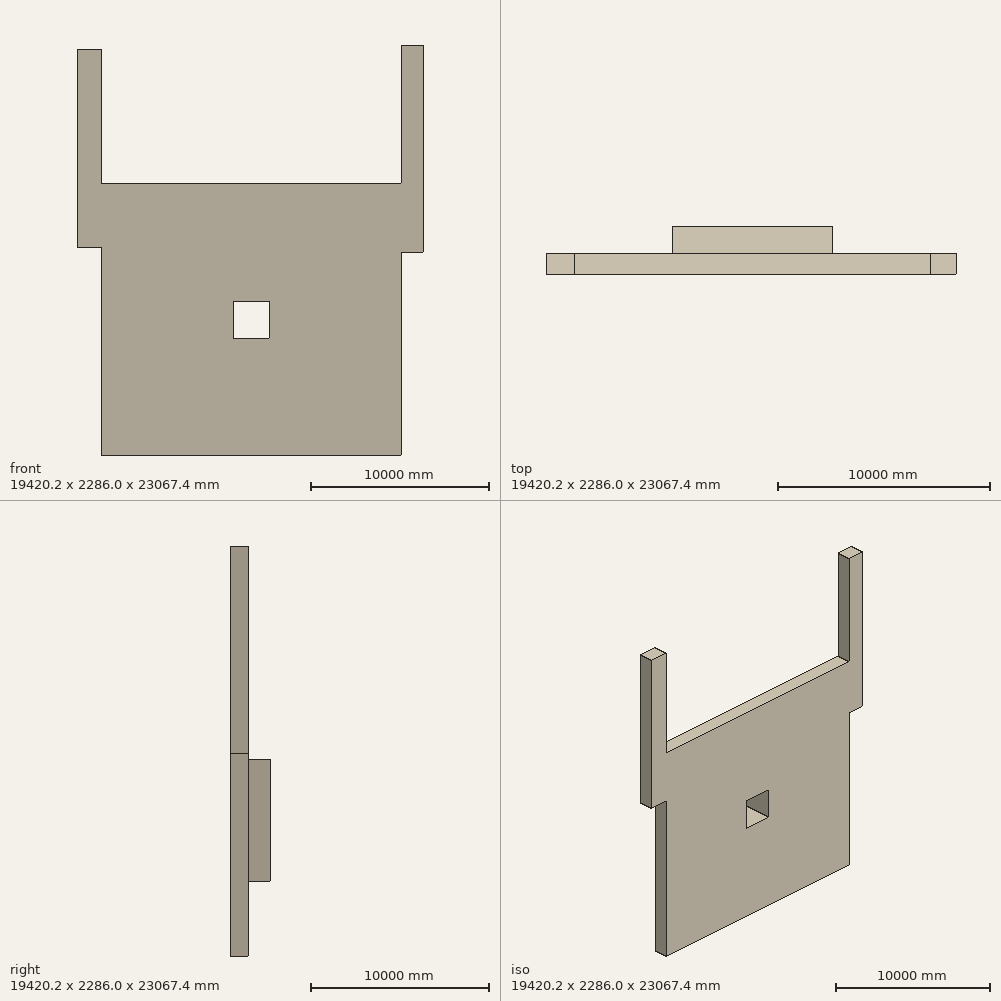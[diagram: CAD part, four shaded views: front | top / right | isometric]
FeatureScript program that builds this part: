
annotation { "Feature Type Name" : "Feature", "Feature Type Description" : "" }
export const myFeature = defineFeature(function(context is Context, id is Id, definition is map)
    precondition{}
    {
        {
            var Q0;
            Q0=qCreatedBy(makeId("Front.planeOp"),FACE);
            var sketch = newSketch(context, id + "F0", { "sketchPlane" : qUnion([Q0])});
            skLineSegment(sketch, "E0.bottom", {"start": v(1035, 1036.8) * mm, "end": v(-1035, 1036.8) * mm});
            skLineSegment(sketch, "E0.top", {"start": v(1035, -1036.8) * mm, "end": v(-1035, -1036.8) * mm});
            skLineSegment(sketch, "E0.left", {"start": v(1035, 1036.8) * mm, "end": v(1035, -1036.8) * mm});
            skLineSegment(sketch, "E0.right", {"start": v(-1035, 1036.8) * mm, "end": v(-1035, -1036.8) * mm});
            skPoint(sketch, "E0.middle", {"position": v(0, 0) * mm});
            skLineSegment(sketch, "E1.bottom", {"start": v(2390.28, 2208.64) * mm, "end": v(-2390.28, 2208.64) * mm});
            skLineSegment(sketch, "E1.top", {"start": v(2390.28, -2208.64) * mm, "end": v(-2390.28, -2208.64) * mm});
            skLineSegment(sketch, "E1.left", {"start": v(2390.28, 2208.64) * mm, "end": v(2390.28, -2208.64) * mm});
            skLineSegment(sketch, "E1.right", {"start": v(-2390.28, 2208.64) * mm, "end": v(-2390.28, -2208.64) * mm});
            skLineSegment(sketch, "E2.bottom", {"start": v(3793.65, 3412.2) * mm, "end": v(-3793.65, 3412.2) * mm});
            skLineSegment(sketch, "E2.top", {"start": v(3793.65, -3412.2) * mm, "end": v(-3793.65, -3412.2) * mm});
            skLineSegment(sketch, "E2.left", {"start": v(3793.65, 3412.2) * mm, "end": v(3793.65, -3412.2) * mm});
            skLineSegment(sketch, "E2.right", {"start": v(-3793.65, 3412.2) * mm, "end": v(-3793.65, -3412.2) * mm});
            skLineSegment(sketch, "E3.bottom", {"start": v(6075.26, 5902.37) * mm, "end": v(-6075.26, 5902.37) * mm});
            skLineSegment(sketch, "E3.top", {"start": v(6075.26, -5902.37) * mm, "end": v(-6075.26, -5902.37) * mm});
            skLineSegment(sketch, "E3.left", {"start": v(6075.26, 5902.37) * mm, "end": v(6075.26, -5902.37) * mm});
            skLineSegment(sketch, "E3.right", {"start": v(-6075.26, 5902.37) * mm, "end": v(-6075.26, -5902.37) * mm});
            skLineSegment(sketch, "E4.bottom", {"start": v(9651.79, 3795.28) * mm, "end": v(8437.94, 3795.28) * mm});
            skLineSegment(sketch, "E4.top", {"start": v(9651.79, 15422.85) * mm, "end": v(8437.94, 15422.85) * mm});
            skLineSegment(sketch, "E4.left", {"start": v(9651.79, 3795.28) * mm, "end": v(9651.79, 15422.85) * mm});
            skLineSegment(sketch, "E4.right", {"start": v(8437.94, 3795.28) * mm, "end": v(8437.94, 15422.85) * mm});
            skPoint(sketch, "E4.middle", {"position": v(9044.86, 9609.06) * mm});
            skLineSegment(sketch, "E5.bottom", {"start": v(8437.94, 7644.55) * mm, "end": v(-8437.94, 7644.55) * mm});
            skLineSegment(sketch, "E5.top", {"start": v(8437.94, -7644.55) * mm, "end": v(-8437.94, -7644.55) * mm});
            skLineSegment(sketch, "E5.left", {"start": v(8437.94, 7644.55) * mm, "end": v(8437.94, -7644.55) * mm});
            skLineSegment(sketch, "E5.right", {"start": v(-8437.94, 7644.55) * mm, "end": v(-8437.94, -7644.55) * mm});
            skLineSegment(sketch, "E6.bottom", {"start": v(-8437.94, 4040.6) * mm, "end": v(-9768.38, 4040.6) * mm});
            skLineSegment(sketch, "E6.top", {"start": v(-8437.94, 15177.53) * mm, "end": v(-9768.38, 15177.53) * mm});
            skLineSegment(sketch, "E6.left", {"start": v(-8437.94, 4040.6) * mm, "end": v(-8437.94, 15177.53) * mm});
            skLineSegment(sketch, "E6.right", {"start": v(-9768.38, 4040.6) * mm, "end": v(-9768.38, 15177.53) * mm});
            skPoint(sketch, "E6.middle", {"position": v(-9103.16, 9609.06) * mm});
            skPoint(sketch, "E6.middle.positionSnap0", {"position": v(8437.94, 9609.06) * mm});
            skPoint(sketch, "E6.centerSnap0", {"position": v(8437.94, 9609.06) * mm});
            skPoint(sketch, "E7.end.orphan", {"position": v(-8437.94, -12888.31) * mm});
            skPoint(sketch, "E8.end.orphan", {"position": v(-7547.34, -12888.31) * mm});
            skPoint(sketch, "E8.start.orphan", {"position": v(-7547.34, -7644.55) * mm});
            skSolve(sketch);
        }
        {
            var Q0;
            Q0 = qSketchRegion(id + "F0", true);
            var Q1;
            Q1=makeQuery(id+"F0.imprint","IMPRINT",FACE,{"disambiguationData":[TD([[makeQuery(id+"F0.imprint","IMPRINT",EDGE,{"derivedFrom":sQuery(id+"F0.wireOp",EDGE,"E2.bottom")}),-1.0]])]});
            var Q2;
            Q2=makeQuery(id+"F0.imprint","IMPRINT",FACE,{"disambiguationData":[TD([[makeQuery(id+"F0.imprint","IMPRINT",EDGE,{"derivedFrom":sQuery(id+"F0.wireOp",EDGE,"E1.bottom")}),-1.0]])]});
            var Q3;
            Q3=makeQuery(id+"F0.imprint","IMPRINT",FACE,{"disambiguationData":[TD([[makeQuery(id+"F0.imprint","IMPRINT",EDGE,{"derivedFrom":sQuery(id+"F0.wireOp",EDGE,"E0.bottom")}),-1.0]])]});
            extrude(context, id + "F1", {"entities" : qUnion([Q0, Q1, Q2, Q3]), "depth" : 2286 * mm});
        }
        {
            var Q0;
            Q0 = qSketchRegion(id + "F0", true);
            var Q1;
            Q1=makeQuery(id+"F0.imprint","IMPRINT",FACE,{"disambiguationData":[TD([[makeQuery(id+"F0.imprint","IMPRINT",EDGE,{"derivedFrom":sQuery(id+"F0.wireOp",EDGE,"E2.bottom")}),-1.0]])]});
            extrude(context, id + "F2", {"entities" : qUnion([Q0, Q1]), "operationType" : NewBodyOperationType.REMOVE, "depth" : 1270 * mm});
        }
    });
